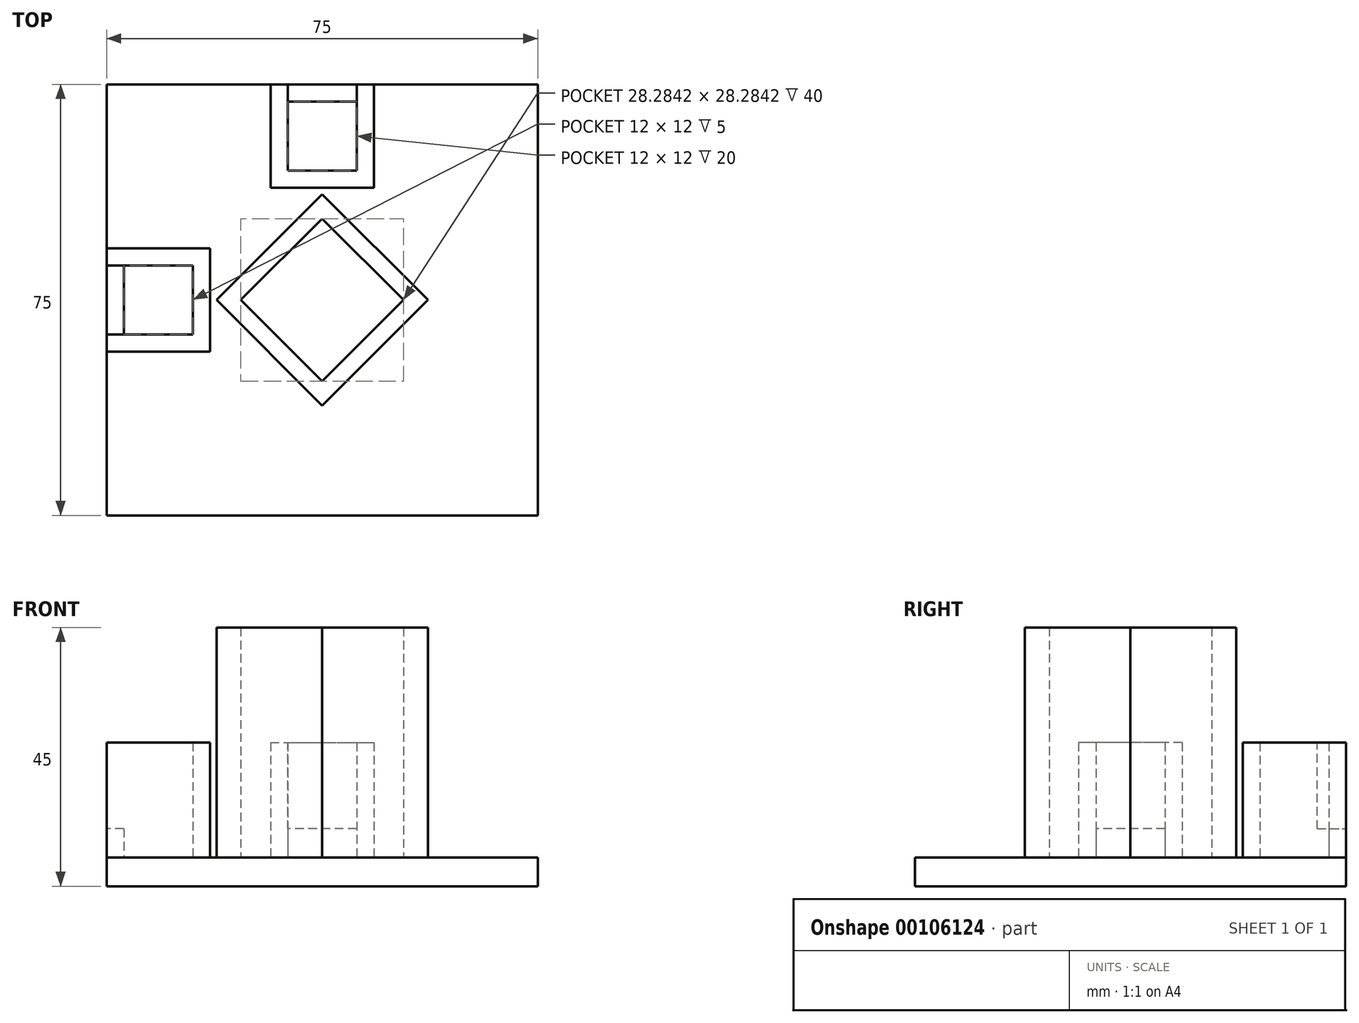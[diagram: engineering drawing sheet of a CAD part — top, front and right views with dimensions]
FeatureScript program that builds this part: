
annotation { "Feature Type Name" : "Feature", "Feature Type Description" : "" }
export const myFeature = defineFeature(function(context is Context, id is Id, definition is map)
    precondition{}
    {
        {
            var Q0;
            Q0=qCreatedBy(makeId("Top.planeOp"),FACE);
            var sketch = newSketch(context, id + "F0", { "sketchPlane" : qUnion([Q0])});
            skLineSegment(sketch, "E0.bottom", {"start": v(-37.5, 37.5) * mm, "end": v(37.5, 37.5) * mm});
            skLineSegment(sketch, "E0.top", {"start": v(-37.5, -37.5) * mm, "end": v(37.5, -37.5) * mm});
            skLineSegment(sketch, "E0.left", {"start": v(-37.5, 37.5) * mm, "end": v(-37.5, -37.5) * mm});
            skLineSegment(sketch, "E0.right", {"start": v(37.5, 37.5) * mm, "end": v(37.5, -37.5) * mm});
            skPoint(sketch, "E0.middle", {"position": v(0, 0) * mm});
            skSolve(sketch);
        }
        {
            var Q0;
            Q0=makeQuery(id+"F0.imprint","IMPRINT",FACE,{"disambiguationData":[TD([[makeQuery(id+"F0.imprint","IMPRINT",EDGE,{"derivedFrom":sQuery(id+"F0.wireOp",EDGE,"E0.bottom")}),-1.0]])]});
            extrude(context, id + "F1", {"entities" : qUnion([Q0]), "depth" : 5 * mm});
        }
        {
            var Q0;
            Q0=makeQuery(id+"F1.opExtrude","CAP_FACE",FACE,{"disambiguationData":[OSD([sQuery(id+"F0.wireOp",EDGE,"E0.bottom"),sQuery(id+"F0.wireOp",EDGE,"E0.top"),sQuery(id+"F0.wireOp",EDGE,"E0.left"),sQuery(id+"F0.wireOp",EDGE,"E0.right")])],"isStart":false});
            var sketch = newSketch(context, id + "F2", { "sketchPlane" : qUnion([Q0])});
            skPoint(sketch, "E1.middle", {"position": v(0, 0) * mm});
            skLineSegment(sketch, "E2", {"start": v(0, 14.14) * mm, "end": v(-14.14, 0) * mm});
            skLineSegment(sketch, "E3", {"start": v(0, 14.14) * mm, "end": v(14.14, 0) * mm});
            skLineSegment(sketch, "E4", {"start": v(14.14, 0) * mm, "end": v(0, -14.14) * mm});
            skLineSegment(sketch, "E5", {"start": v(0, -14.14) * mm, "end": v(-14.14, 0) * mm});
            skLineSegment(sketch, "E6.0", {"start": v(0, 18.38) * mm, "end": v(-18.38, 0) * mm});
            skLineSegment(sketch, "E6.1", {"start": v(0, 18.38) * mm, "end": v(18.38, 0) * mm});
            skLineSegment(sketch, "E6.2", {"start": v(18.38, 0) * mm, "end": v(0, -18.38) * mm});
            skLineSegment(sketch, "E6.3", {"start": v(0, -18.38) * mm, "end": v(-18.38, 0) * mm});
            skSolve(sketch);
        }
        {
            var Q0;
            Q0=makeQuery(id+"F2.imprint","IMPRINT",FACE,{"disambiguationData":[TD([[makeQuery(id+"F2.imprint","IMPRINT",EDGE,{"derivedFrom":sQuery(id+"F2.wireOp",EDGE,"E2")}),-1.0]])]});
            extrude(context, id + "F3", {"entities" : qUnion([Q0]), "operationType" : NewBodyOperationType.ADD, "depth" : 40 * mm});
        }
        {
            var Q0;
            {var subQ0=sQuery(id+"F0.wireOp",EDGE,"E0.right");var subQ1=sQuery(id+"F0.wireOp",EDGE,"E0.left");var subQ2=sQuery(id+"F0.wireOp",EDGE,"E0.top");var subQ3=sQuery(id+"F0.wireOp",EDGE,"E0.bottom");Q0=makeQuery(id+"F3.boolean.opBoolean","SPLIT",FACE,{"disambiguationData":[TD([makeQuery(id+"F1.opExtrude","SWEPT_FACE",FACE,{"disambiguationData":[OSD([subQ3])]})])],"derivedFrom":makeQuery(id+"F1.opExtrude","CAP_FACE",FACE,{"disambiguationData":[OSD([subQ3,subQ2,subQ1,subQ0])],"isStart":false})});}
            var sketch = newSketch(context, id + "F4", { "sketchPlane" : qUnion([Q0])});
            skLineSegment(sketch, "E7.bottom", {"start": v(-37.5, 9) * mm, "end": v(-19.5, 9) * mm});
            skLineSegment(sketch, "E7.top", {"start": v(-37.5, -9) * mm, "end": v(-19.5, -9) * mm});
            skLineSegment(sketch, "E7.left", {"start": v(-37.5, 9) * mm, "end": v(-37.5, -9) * mm});
            skLineSegment(sketch, "E7.right", {"start": v(-19.5, 9) * mm, "end": v(-19.5, -9) * mm});
            skPoint(sketch, "E7.middle", {"position": v(-28.5, 0) * mm});
            skPoint(sketch, "E7.middle.positionSnap0", {"position": v(-37.5, 0) * mm});
            skPoint(sketch, "E7.centerSnap0", {"position": v(-37.5, 0) * mm});
            skLineSegment(sketch, "E8.0", {"start": v(-34.5, 6) * mm, "end": v(-22.5, 6) * mm});
            skLineSegment(sketch, "E8.1", {"start": v(-34.5, 6) * mm, "end": v(-34.5, -6) * mm});
            skLineSegment(sketch, "E8.2", {"start": v(-34.5, -6) * mm, "end": v(-22.5, -6) * mm});
            skLineSegment(sketch, "E8.3", {"start": v(-22.5, 6) * mm, "end": v(-22.5, -6) * mm});
            skLineSegment(sketch, "E9.bottom", {"start": v(-8.97, 37.51) * mm, "end": v(9.03, 37.51) * mm});
            skLineSegment(sketch, "E9.top", {"start": v(-8.97, 19.51) * mm, "end": v(9.03, 19.51) * mm});
            skLineSegment(sketch, "E9.left", {"start": v(-8.97, 37.51) * mm, "end": v(-8.97, 19.51) * mm});
            skLineSegment(sketch, "E9.right", {"start": v(9.03, 37.51) * mm, "end": v(9.03, 19.51) * mm});
            skPoint(sketch, "E9.middle", {"position": v(0.03, 28.51) * mm});
            skPoint(sketch, "E9.middle.positionSnap0", {"position": v(-8.97, 28.51) * mm});
            skPoint(sketch, "E9.centerSnap0", {"position": v(-8.97, 28.51) * mm});
            skLineSegment(sketch, "E10.0", {"start": v(-5.97, 34.51) * mm, "end": v(6.03, 34.51) * mm});
            skLineSegment(sketch, "E10.1", {"start": v(-5.97, 34.51) * mm, "end": v(-5.97, 22.51) * mm});
            skLineSegment(sketch, "E10.2", {"start": v(-5.97, 22.51) * mm, "end": v(6.03, 22.51) * mm});
            skLineSegment(sketch, "E10.3", {"start": v(6.03, 34.51) * mm, "end": v(6.03, 22.51) * mm});
            skSolve(sketch);
        }
        {
            var Q0;
            {var subQ1=sQuery(id+"F4.wireOp",EDGE,"E9.top");Q0=makeQuery(id+"F4.imprint","IMPRINT",FACE,{"disambiguationData":[TD([[makeQuery(id+"F4.imprint","IMPRINT",EDGE,{"derivedFrom":subQ1}),1.0]])]});}
            var Q1;
            Q1=makeQuery(id+"F4.imprint","IMPRINT",FACE,{"disambiguationData":[TD([[makeQuery(id+"F4.imprint","IMPRINT",EDGE,{"derivedFrom":sQuery(id+"F4.wireOp",EDGE,"E7.bottom")}),-1.0]])]});
            extrude(context, id + "F5", {"entities" : qUnion([Q0, Q1]), "operationType" : NewBodyOperationType.ADD, "depth" : 5 * mm});
        }
        {
            var Q0;
            Q0=makeQuery(id+"F5.opExtrude","CAP_FACE",FACE,{"disambiguationData":[OSD([sQuery(id+"F0.wireOp",EDGE,"E0.bottom"),sQuery(id+"F4.wireOp",EDGE,"E9.top"),sQuery(id+"F4.wireOp",EDGE,"E9.left"),sQuery(id+"F4.wireOp",EDGE,"E9.right"),sQuery(id+"F4.wireOp",EDGE,"E10.0"),sQuery(id+"F4.wireOp",EDGE,"E10.1"),sQuery(id+"F4.wireOp",EDGE,"E10.2"),sQuery(id+"F4.wireOp",EDGE,"E10.3")])],"isStart":false});
            var Q1;
            Q1=makeQuery(id+"F5.opExtrude","CAP_FACE",FACE,{"disambiguationData":[OSD([sQuery(id+"F4.wireOp",EDGE,"E7.bottom"),sQuery(id+"F4.wireOp",EDGE,"E7.top"),sQuery(id+"F4.wireOp",EDGE,"E7.left"),sQuery(id+"F4.wireOp",EDGE,"E7.right"),sQuery(id+"F4.wireOp",EDGE,"E8.0"),sQuery(id+"F4.wireOp",EDGE,"E8.1"),sQuery(id+"F4.wireOp",EDGE,"E8.2"),sQuery(id+"F4.wireOp",EDGE,"E8.3")])],"isStart":false});
            extrude(context, id + "F6", {"entities" : qUnion([Q0, Q1]), "operationType" : NewBodyOperationType.ADD, "depth" : 15 * mm});
        }
        {
            var Q0;
            {var subQ0=sQuery(id+"F4.wireOp",EDGE,"E7.left");Q0=makeQuery(id+"F6.boolean.opBoolean","MERGE",FACE,{"derivedFrom":[makeQuery(id+"F5.boolean.opBoolean","MERGE",FACE,{"derivedFrom":[makeQuery(id+"F1.opExtrude","SWEPT_FACE",FACE,{"disambiguationData":[OSD([sQuery(id+"F0.wireOp",EDGE,"E0.left")])]}),makeQuery(id+"F5.opExtrude","SWEPT_FACE",FACE,{"disambiguationData":[OSD([subQ0])]})]}),makeQuery(id+"F6.opExtrude","SWEPT_FACE",FACE,{"disambiguationData":[OSD([subQ0])]})]});}
            var sketch = newSketch(context, id + "F7", { "sketchPlane" : qUnion([Q0])});
            skLineSegment(sketch, "E11.bottom", {"start": v(-6, 25) * mm, "end": v(6, 25) * mm});
            skLineSegment(sketch, "E11.top", {"start": v(-6, 10) * mm, "end": v(6, 10) * mm});
            skLineSegment(sketch, "E11.left", {"start": v(-6, 25) * mm, "end": v(-6, 10) * mm});
            skLineSegment(sketch, "E11.right", {"start": v(6, 25) * mm, "end": v(6, 10) * mm});
            skPoint(sketch, "E11.middle", {"position": v(0, 17.5) * mm});
            skSolve(sketch);
        }
        {
            var Q0;
            Q0=makeQuery(id+"F7.imprint","IMPRINT",FACE,{"disambiguationData":[TD([[makeQuery(id+"F7.imprint","IMPRINT",EDGE,{"derivedFrom":sQuery(id+"F7.wireOp",EDGE,"E11.bottom")}),-1.0]])]});
            extrude(context, id + "F8", {"entities" : qUnion([Q0]), "operationType" : NewBodyOperationType.REMOVE, "oppositeDirection" : true, "depth" : 5 * mm});
        }
        {
            var Q0;
            {var subQ0=sQuery(id+"F0.wireOp",EDGE,"E0.bottom");Q0=makeQuery(id+"F6.boolean.opBoolean","MERGE",FACE,{"derivedFrom":[makeQuery(id+"F5.boolean.opBoolean","MERGE",FACE,{"derivedFrom":[makeQuery(id+"F1.opExtrude","SWEPT_FACE",FACE,{"disambiguationData":[OSD([subQ0])]}),makeQuery(id+"F5.opExtrude","SWEPT_FACE",FACE,{"disambiguationData":[OSD([subQ0])]})]}),makeQuery(id+"F6.opExtrude","SWEPT_FACE",FACE,{"disambiguationData":[OSD([subQ0])]})]});}
            var sketch = newSketch(context, id + "F9", { "sketchPlane" : qUnion([Q0])});
            skLineSegment(sketch, "E12.bottom", {"start": v(-6, 25) * mm, "end": v(6, 25) * mm});
            skLineSegment(sketch, "E12.top", {"start": v(-6, 10) * mm, "end": v(6, 10) * mm});
            skLineSegment(sketch, "E12.left", {"start": v(-6, 25) * mm, "end": v(-6, 10) * mm});
            skLineSegment(sketch, "E12.right", {"start": v(6, 25) * mm, "end": v(6, 10) * mm});
            skPoint(sketch, "E12.middle", {"position": v(0, 17.5) * mm});
            skSolve(sketch);
        }
        {
            var Q0;
            Q0=makeQuery(id+"F9.imprint","IMPRINT",FACE,{"disambiguationData":[TD([[makeQuery(id+"F9.imprint","IMPRINT",EDGE,{"derivedFrom":sQuery(id+"F9.wireOp",EDGE,"E12.bottom")}),1.0]])]});
            extrude(context, id + "F10", {"entities" : qUnion([Q0]), "operationType" : NewBodyOperationType.REMOVE, "oppositeDirection" : true, "depth" : 5 * mm});
        }
    });
